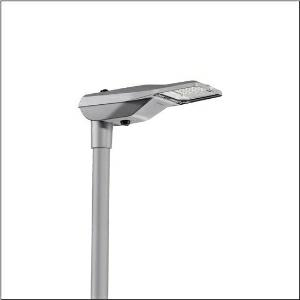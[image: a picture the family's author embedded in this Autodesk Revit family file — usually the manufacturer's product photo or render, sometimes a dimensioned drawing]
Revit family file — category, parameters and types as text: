
# Revit family: streetlight_sl_21_micro___st0_8a_5xe1c33t08db_e381
name_source: partatom
category: Lighting Fixtures
units: mm (PartAtom-declared; Revit-internal decimal feet)

## family parameters
Cut with Voids When Loaded = No
Host = Face
Light Source = No
Part Type = Normal
Room Calculation Point = No
Round Connector Dimension = Use Diameter
Shared = No

## types (1)
- --- (1 x LED, 5110 lm, 39.1 W, 3000K)
    Apparent Load = 39 VA
    CIE Flux Codes = 38 75 97 100 100
    Color Rendering = 70
    Color Temperature = 3000K
    Default Elevation = 1800 mm
    Description = Streetlight SL 21 micro, mast luminaire, primary light control with lens, of PMMA, primary optical cover: cover, of toughened safety glass, transparent, light distribution: ST0.8a, light emission: direct distribution, primary light characteristic: asymmetric, installation type: side-entry, post-top, LED, High Power LED, rated luminous flux: 5.110lm, luminous efficacy: 131lm/W, light colour: 730, colour temperature: 3000K, control gear: D4i, control: flexible luminous flux parameterisation, time-dependent luminous flux control, constant luminous flux control, overheat protection, pre-setting: logarithmic dimming characteristic, mains connection: 220..240V, AC, 50/60Hz, start of lifetime: 39W, end of service life: 41W, reduction: 18W, luminaire housing, of diecast aluminium, powder-coated, SITECO metallic grey (DB 702S), corrosivity category C5 high according to DIN EN ISO 12944, please order mast flange separately, inclination adjustable: 0°, 5°, 10°, 15°, sealing non-destructively replaceable, multi-level sealing system, length: 528mm, width: 235mm, height: 110mm, mast flange for spigot size: 42mm (side-entry): 5XC10008XM4, 60/48mm (side-entry/post-top): 5XC10108XM2, 76/60mm (side-entry/post-top): 5XC10108XM1, Smart Interface below and above, protection rating (complete): IP66, insulation class (complete): insulation class II (safety insulation), certification: CE, ENEC, ENEC+, VDE, impact resistance: IK10, permissible operating ambient temperature for outdoor applications: -40..+50°C, standard-compliant lighting for roads and squares, packaging unit: 1 piece

Light Distribution: ST0.8a
    Height = 110 mm
    Lamp = 1 x LED
    Lamp Light Flux = 5110 lm
    Lamp Power = 39.1 W
    Lamp count = 1
    Length = 528 mm
    Luminous efficacy = 131 lm/W
    Manufacturer = Siteco
    ModVariant = No
    Model = 5XE1C33T08DB
    Number of Poles = 1
    OnlyDefault = Yes
    Power Factor = 1
    Product Name = Streetlight SL 21 micro | ST0.8a
    Product group = mast luminaire | pylon top
    ProductGroupID = 6100
    Protection Class = Protection class II
    Protection Degree = IP 66
    RLX_Detail_Level = 1
    RLX_Emergency_Light_Flux = 0 lm
    RLX_Emergency_Type = 0
    RLX_Emergency_Type_DB = No
    RlxData = <blob elided: 98577 chars, md5=90ef7f9b>
    Socket = socket
    Standby Power = 0 W
    System Light Flux = 5110 lm
    System Power = 39 W
    Type Comments = factory setting: luminous flux: 100 % | dim-lin: 254 | 765 mA
    Type Image = l_1007239.jpg
    URL = http://relux.com
    VarID = @adj_153843
    Voltage = 0 V
    Weight = 0.00 kg
    Width = 235 mm

## geometry (parser evidence)
native form markers: Blend x4, Sweep x10
no freeform markers — native parametric forms only
